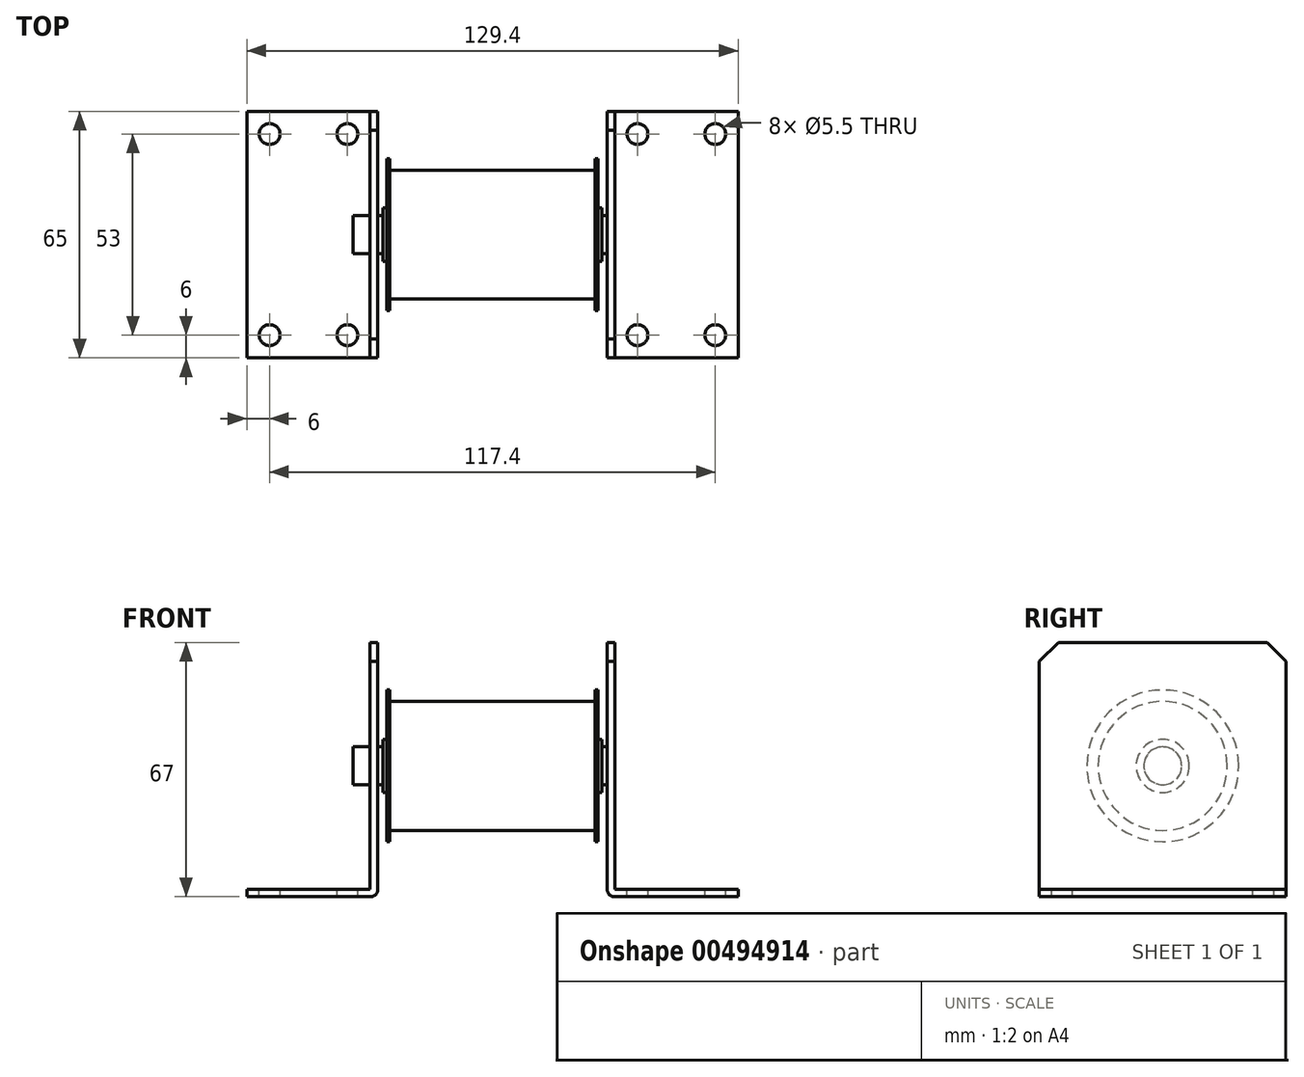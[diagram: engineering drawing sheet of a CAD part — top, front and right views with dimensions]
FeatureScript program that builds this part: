
annotation { "Feature Type Name" : "Feature", "Feature Type Description" : "" }
export const myFeature = defineFeature(function(context is Context, id is Id, definition is map)
    precondition{}
    {
        {
            var Q0;
            Q0=qCreatedBy(makeId("Right.planeOp"),FACE);
            var sketch = newSketch(context, id + "F0", { "sketchPlane" : qUnion([Q0])});
            skCircle(sketch, "E0", {"center": v(0, 0) * mm, "radius": 20 * mm});
            skSolve(sketch);
        }
        {
            var Q0;
            Q0=qSketchRegion(id+"F0",true);
            extrude(context, id + "F1", {"entities" : qUnion([Q0]), "depth" : 27.8 * mm, "hasSecondDirection" : true, "secondDirectionOppositeDirection" : true, "secondDirectionDepth" : 27.8 * mm});
        }
        {
            var Q0;
            Q0=qCreatedBy(makeId("Right.planeOp"),FACE);
            var sketch = newSketch(context, id + "F2", { "sketchPlane" : qUnion([Q0])});
            skCircle(sketch, "E1", {"center": v(0, 0) * mm, "radius": 7 * mm});
            skSolve(sketch);
        }
        {
            var Q0;
            Q0=qSketchRegion(id+"F2",true);
            extrude(context, id + "F3", {"entities" : qUnion([Q0]), "operationType" : NewBodyOperationType.ADD, "depth" : 28.8 * mm, "hasSecondDirection" : true, "secondDirectionOppositeDirection" : true, "secondDirectionDepth" : 28.8 * mm});
        }
        {
            var Q0;
            Q0=qCreatedBy(makeId("Right.planeOp"),FACE);
            var sketch = newSketch(context, id + "F4", { "sketchPlane" : qUnion([Q0])});
            skCircle(sketch, "E2", {"center": v(0, 0) * mm, "radius": 17 * mm});
            skCircle(sketch, "E3", {"center": v(0, 0) * mm, "radius": 20 * mm});
            skSolve(sketch);
        }
        {
            var Q0;
            Q0=qSketchRegion(id+"F4",true);
            extrude(context, id + "F5", {"entities" : qUnion([Q0]), "operationType" : NewBodyOperationType.REMOVE, "oppositeDirection" : true, "depth" : 27 * mm, "hasSecondDirection" : true, "secondDirectionOppositeDirection" : false, "secondDirectionDepth" : 27 * mm});
        }
        {
            var Q0;
            Q0=qCreatedBy(makeId("Right.planeOp"),FACE);
            var sketch = newSketch(context, id + "F6", { "sketchPlane" : qUnion([Q0])});
            skCircle(sketch, "E4", {"center": v(0, 0) * mm, "radius": 5 * mm});
            skSolve(sketch);
        }
        {
            var Q0;
            Q0=qSketchRegion(id+"F6",true);
            extrude(context, id + "F7", {"entities" : qUnion([Q0]), "operationType" : NewBodyOperationType.ADD, "depth" : 32.2 * mm, "hasSecondDirection" : true, "secondDirectionOppositeDirection" : true, "secondDirectionDepth" : 36.7 * mm});
        }
        {
            var Q0;
            Q0=qCreatedBy(makeId("Front.planeOp"),FACE);
            var sketch = newSketch(context, id + "F8", { "sketchPlane" : qUnion([Q0])});
            skLineSegment(sketch, "E5", {"start": v(30.2, 32.5) * mm, "end": v(30.2, -34.5) * mm});
            skLineSegment(sketch, "E6", {"start": v(30.2, -34.5) * mm, "end": v(64.7, -34.5) * mm});
            skLineSegment(sketch, "E7", {"start": v(64.7, -34.5) * mm, "end": v(64.7, -32.5) * mm});
            skLineSegment(sketch, "E8", {"start": v(64.7, -32.5) * mm, "end": v(32.2, -32.5) * mm});
            skLineSegment(sketch, "E9", {"start": v(32.2, -32.5) * mm, "end": v(32.2, 32.5) * mm});
            skLineSegment(sketch, "E10", {"start": v(32.2, 32.5) * mm, "end": v(30.2, 32.5) * mm});
            skLineSegment(sketch, "E11", {"start": v(-30.2, 32.5) * mm, "end": v(-30.2, -34.5) * mm});
            skLineSegment(sketch, "E12", {"start": v(-30.2, -34.5) * mm, "end": v(-64.7, -34.5) * mm});
            skLineSegment(sketch, "E13", {"start": v(-64.7, -34.5) * mm, "end": v(-64.7, -32.5) * mm});
            skLineSegment(sketch, "E14", {"start": v(-64.7, -32.5) * mm, "end": v(-32.2, -32.5) * mm});
            skLineSegment(sketch, "E15", {"start": v(-32.2, -32.5) * mm, "end": v(-32.2, 32.5) * mm});
            skLineSegment(sketch, "E16", {"start": v(-32.2, 32.5) * mm, "end": v(-30.2, 32.5) * mm});
            skSolve(sketch);
        }
        {
            var Q0;
            Q0=qSketchRegion(id+"F8",true);
            extrude(context, id + "F9", {"entities" : qUnion([Q0]), "operationType" : NewBodyOperationType.ADD, "depth" : 32.5 * mm, "hasSecondDirection" : true, "secondDirectionOppositeDirection" : true, "secondDirectionDepth" : 32.5 * mm});
        }
        {
            var Q0;
            Q0=makeQuery(id+"F9.opExtrude","CAP_EDGE",EDGE,{"disambiguationData":[OSD([sQuery(id+"F8.wireOp",EDGE,"E10")])],"isStart":false});
            var Q1;
            Q1=makeQuery(id+"F9.opExtrude","CAP_EDGE",EDGE,{"disambiguationData":[OSD([sQuery(id+"F8.wireOp",EDGE,"E10")])],"isStart":true});
            var Q2;
            Q2=makeQuery(id+"F9.opExtrude","CAP_EDGE",EDGE,{"disambiguationData":[OSD([sQuery(id+"F8.wireOp",EDGE,"E16")])],"isStart":false});
            var Q3;
            Q3=makeQuery(id+"F9.opExtrude","CAP_EDGE",EDGE,{"disambiguationData":[OSD([sQuery(id+"F8.wireOp",EDGE,"E16")])],"isStart":true});
            chamfer(context, id + "F10", {"entities" : qUnion([Q0, Q1, Q2, Q3]), "width" : 5 * mm, "tangentPropagation" : true});
        }
        {
            var Q0;
            Q0=makeQuery(id+"F9.opExtrude","SWEPT_EDGE",EDGE,{"disambiguationData":[OSD([sQuery(id+"F8.wireOp",EDGE,"E5"),sQuery(id+"F8.wireOp",EDGE,"E6")])]});
            var Q1;
            Q1=makeQuery(id+"F9.opExtrude","SWEPT_EDGE",EDGE,{"disambiguationData":[OSD([sQuery(id+"F8.wireOp",EDGE,"E11"),sQuery(id+"F8.wireOp",EDGE,"E12")])]});
            fillet(context, id + "F11", {"entities" : qUnion([Q0, Q1]), "radius" : 2 * mm, "tangentPropagation" : true, "allowEdgeOverflow" : false});
        }
        {
            var Q0;
            Q0=makeQuery(id+"F9.opExtrude","SWEPT_FACE",FACE,{"disambiguationData":[OSD([sQuery(id+"F8.wireOp",EDGE,"E8")])]});
            var sketch = newSketch(context, id + "F12", { "sketchPlane" : qUnion([Q0])});
            skPoint(sketch, "E17", {"position": v(-58.7, 26.5) * mm});
            skPoint(sketch, "E18", {"position": v(-58.7, -26.5) * mm});
            skPoint(sketch, "E19", {"position": v(58.7, -26.5) * mm});
            skPoint(sketch, "E20", {"position": v(58.7, 26.5) * mm});
            skPoint(sketch, "E21", {"position": v(38.2, 26.5) * mm});
            skPoint(sketch, "E22", {"position": v(38.2, -26.5) * mm});
            skPoint(sketch, "E23", {"position": v(-38.2, 26.5) * mm});
            skPoint(sketch, "E24", {"position": v(-38.2, -26.5) * mm});
            skSolve(sketch);
        }
        {
            var Q0;
            Q0=sQuery(id+"F12.wireOp",VERTEX,"E21");
            var Q1;
            Q1=sQuery(id+"F12.wireOp",VERTEX,"E22");
            var Q2;
            Q2=sQuery(id+"F12.wireOp",VERTEX,"E19");
            var Q3;
            Q3=sQuery(id+"F12.wireOp",VERTEX,"E24");
            var Q4;
            Q4=sQuery(id+"F12.wireOp",VERTEX,"E18");
            var Q5;
            Q5=sQuery(id+"F12.wireOp",VERTEX,"E17");
            var Q6;
            Q6=sQuery(id+"F12.wireOp",VERTEX,"E23");
            var Q7;
            Q7=sQuery(id+"F12.wireOp",VERTEX,"E20");
            var Q8;
            Q8=makeQuery(id+"F1.opExtrude","SWEPT_BODY",BODY,{"disambiguationData":[OSD([sQuery(id+"F0.wireOp",EDGE,"E0")])]});
            hole(context, id + "F13", {"style" : HoleStyle.SIMPLE, "endStyle" : HoleEndStyle.THROUGH, "standardTappedOrClearance" : lookupTablePath({ "standard" : "ISO", "size" : "5.5", "type" : "Drilled" }), "standardBlindInLast" : lookupTablePath({ "standard" : "ISO", "size" : "5.5", "type" : "Drilled" }), "holeDiameter" : 5.5 * mm, "isTappedThrough" : true, "tappedDepth" : 10 * mm, "tapClearance" : 3, "locations" : qUnion([Q0, Q1, Q2, Q3, Q4, Q5, Q6, Q7]), "scope" : qUnion([Q8])});
        }
    });
